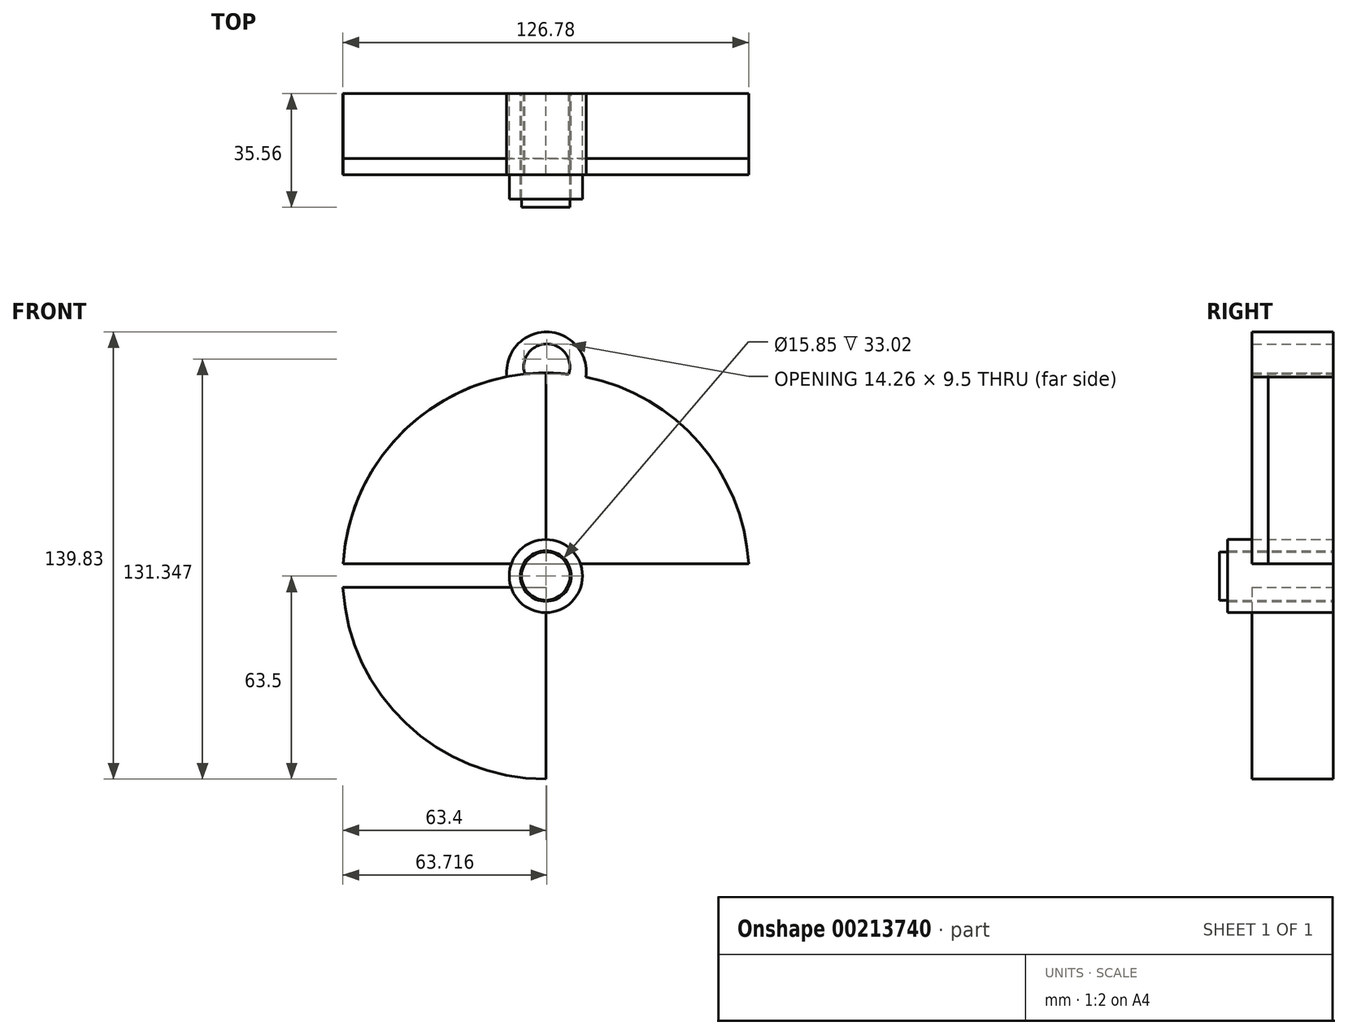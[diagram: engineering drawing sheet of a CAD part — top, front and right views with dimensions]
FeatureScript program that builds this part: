
annotation { "Feature Type Name" : "Feature", "Feature Type Description" : "" }
export const myFeature = defineFeature(function(context is Context, id is Id, definition is map)
    precondition{}
    {
        {
            var Q0;
            Q0=qCreatedBy(makeId("Front.planeOp"),FACE);
            var sketch = newSketch(context, id + "F0", { "sketchPlane" : qUnion([Q0])});
            skCircle(sketch, "E0", {"center": v(0, 0) * mm, "radius": 63.5 * mm});
            skLineSegment(sketch, "E1", {"start": v(-66.18, 3.85) * mm, "end": v(67.6, 3.85) * mm});
            skLineSegment(sketch, "E2", {"start": v(-66.18, -3.57) * mm, "end": v(68.74, -3.57) * mm});
            skLineSegment(sketch, "E3", {"start": v(0, 68.32) * mm, "end": v(0, -70.6) * mm});
            skArc(sketch, "E4", {"start": v(12.53, 62.25) * mm, "mid": v(0.24, 76.33) * mm, "end": v(-12.14, 62.33) * mm});
            skArc(sketch, "E5", {"start": v(7.16, 63.1) * mm, "mid": v(0.34, 72.6) * mm, "end": v(-6.56, 63.16) * mm});
            skSolve(sketch);
        }
        {
            var Q0;
            Q0=qCreatedBy(makeId("Front.planeOp"),FACE);
            var sketch = newSketch(context, id + "F1", { "sketchPlane" : qUnion([Q0])});
            skCircle(sketch, "E6", {"center": v(0, 0) * mm, "radius": 11.43 * mm});
            skCircle(sketch, "E7", {"center": v(0, 0) * mm, "radius": 7.93 * mm});
            skSolve(sketch);
        }
        {
            var Q0;
            Q0 = qSketchRegion(id + "F1", true);
            extrude(context, id + "F2", {"entities" : qUnion([Q0]), "depth" : 33.02 * mm});
        }
        {
            var Q0;
            {var subQ0=sQuery(id+"F0.wireOp",EDGE,"E1");var subQ1=sQuery(id+"F0.wireOp",EDGE,"E0");var subQ2=makeQuery(id+"F0.imprint","INTERSECT",VERTEX,{"disambiguationData":[OD(1.0)],"derivedFrom":[subQ1,subQ0]});Q0=makeQuery(id+"F0.imprint","IMPRINT",FACE,{"disambiguationData":[TD([[makeQuery(id+"F0.imprint","IMPRINT",EDGE,{"disambiguationData":[TD([[subQ2,-1.0]])],"derivedFrom":subQ1}),1.0]])]});}
            var Q1;
            {var subQ0=sQuery(id+"F0.wireOp",EDGE,"E1");var subQ1=sQuery(id+"F0.wireOp",EDGE,"E0");var subQ2=makeQuery(id+"F0.imprint","INTERSECT",VERTEX,{"disambiguationData":[OD(0.0)],"derivedFrom":[subQ1,subQ0]});Q1=makeQuery(id+"F0.imprint","IMPRINT",FACE,{"disambiguationData":[TD([[makeQuery(id+"F0.imprint","IMPRINT",EDGE,{"disambiguationData":[TD([[subQ2,1.0]])],"derivedFrom":subQ1}),1.0]])]});}
            extrude(context, id + "F3", {"entities" : qUnion([Q0, Q1]), "depth" : 20.32 * mm});
        }
        {
            var Q0;
            {var subQ1=sQuery(id+"F0.wireOp",EDGE,"E0");var subQ5=makeQuery(id+"F0.imprint","INTERSECT",VERTEX,{"disambiguationData":[OD(1.0)],"derivedFrom":[subQ1,sQuery(id+"F0.wireOp",EDGE,"E5")]});Q0=makeQuery(id+"F0.imprint","IMPRINT",FACE,{"disambiguationData":[TD([[makeQuery(id+"F0.imprint","IMPRINT",EDGE,{"disambiguationData":[TD([[subQ5,1.0]])],"derivedFrom":subQ1}),1.0]])]});}
            var Q1;
            {var subQ1=sQuery(id+"F0.wireOp",EDGE,"E0");var subQ7=makeQuery(id+"F0.imprint","INTERSECT",VERTEX,{"disambiguationData":[OD(0.0)],"derivedFrom":[subQ1,sQuery(id+"F0.wireOp",EDGE,"E4")]});Q1=makeQuery(id+"F0.imprint","IMPRINT",FACE,{"disambiguationData":[TD([[makeQuery(id+"F0.imprint","IMPRINT",EDGE,{"disambiguationData":[TD([[subQ7,1.0]])],"derivedFrom":subQ1}),1.0]])]});}
            var Q2;
            {var subQ0=sQuery(id+"F0.wireOp",EDGE,"E4");Q2=makeQuery(id+"F0.imprint","IMPRINT",FACE,{"disambiguationData":[TD([[makeQuery(id+"F0.imprint","IMPRINT",EDGE,{"derivedFrom":subQ0}),1.0]])]});}
            extrude(context, id + "F4", {"entities" : qUnion([Q0, Q1, Q2]), "depth" : 25.4 * mm});
        }
        {
            var Q0;
            {var subQ0=sQuery(id+"F0.wireOp",EDGE,"E2");var subQ1=sQuery(id+"F0.wireOp",EDGE,"E0");var subQ2=makeQuery(id+"F0.imprint","INTERSECT",VERTEX,{"disambiguationData":[OD(0.0)],"derivedFrom":[subQ1,subQ0]});Q0=makeQuery(id+"F0.imprint","IMPRINT",FACE,{"disambiguationData":[TD([[makeQuery(id+"F0.imprint","IMPRINT",EDGE,{"disambiguationData":[TD([[subQ2,-1.0]])],"derivedFrom":subQ1}),1.0]])]});}
            var Q1;
            {var subQ0=sQuery(id+"F0.wireOp",EDGE,"E3");var subQ1=sQuery(id+"F0.wireOp",EDGE,"E0");var subQ2=makeQuery(id+"F0.imprint","INTERSECT",VERTEX,{"disambiguationData":[OD(0.0)],"derivedFrom":[subQ1,subQ0]});Q1=makeQuery(id+"F0.imprint","IMPRINT",FACE,{"disambiguationData":[TD([[makeQuery(id+"F0.imprint","IMPRINT",EDGE,{"disambiguationData":[TD([[subQ2,-1.0]])],"derivedFrom":subQ1}),1.0]])]});}
            extrude(context, id + "F5", {"entities" : qUnion([Q0, Q1]), "depth" : 25.4 * mm});
        }
        {
            var Q0;
            Q0=qCreatedBy(makeId("Front.planeOp"),FACE);
            var sketch = newSketch(context, id + "F6", { "sketchPlane" : qUnion([Q0])});
            skCircle(sketch, "E8", {"center": v(0, 0) * mm, "radius": 7.55 * mm});
            skSolve(sketch);
        }
        {
            var Q0;
            Q0 = qSketchRegion(id + "F6", true);
            extrude(context, id + "F7", {"entities" : qUnion([Q0]), "depth" : 35.56 * mm});
        }
    });
